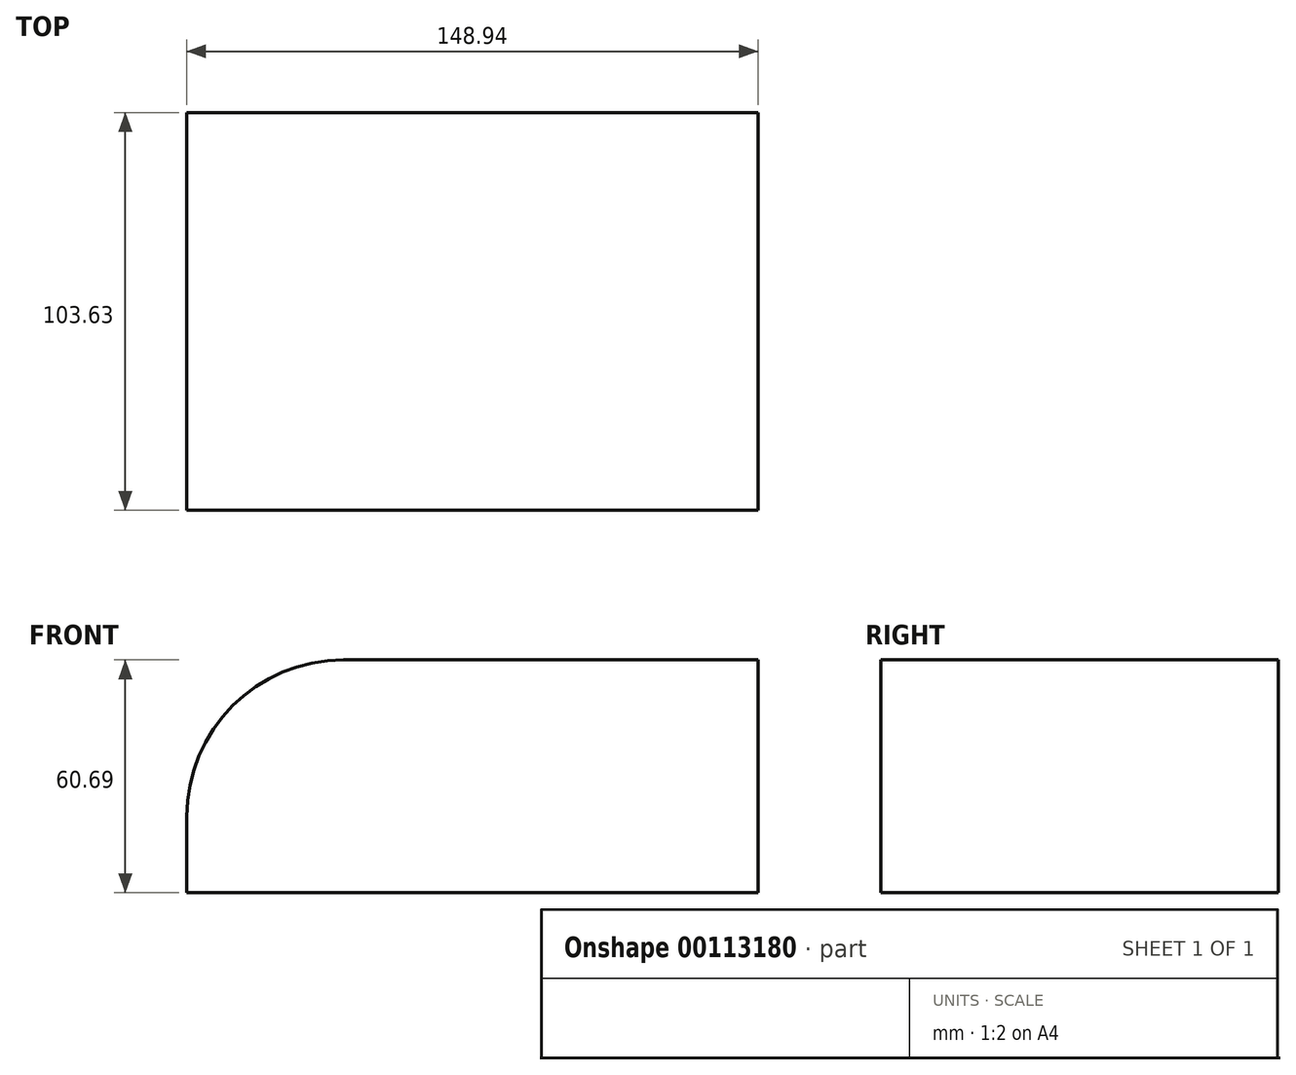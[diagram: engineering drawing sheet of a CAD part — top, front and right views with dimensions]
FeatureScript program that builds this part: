
annotation { "Feature Type Name" : "Feature", "Feature Type Description" : "" }
export const myFeature = defineFeature(function(context is Context, id is Id, definition is map)
    precondition{}
    {
        {
            var Q0;
            Q0=qCreatedBy(makeId("Top.planeOp"),FACE);
            var sketch = newSketch(context, id + "F0", { "sketchPlane" : qUnion([Q0])});
            skLineSegment(sketch, "E0.bottom", {"start": v(-84.58, 52.04) * mm, "end": v(64.36, 52.04) * mm});
            skLineSegment(sketch, "E0.top", {"start": v(-84.58, -51.6) * mm, "end": v(64.36, -51.6) * mm});
            skLineSegment(sketch, "E0.left", {"start": v(-84.58, 52.04) * mm, "end": v(-84.58, -51.6) * mm});
            skLineSegment(sketch, "E0.right", {"start": v(64.36, 52.04) * mm, "end": v(64.36, -51.6) * mm});
            skSolve(sketch);
        }
        {
            var Q0;
            Q0 = qSketchRegion(id + "F0", true);
            extrude(context, id + "F1", {"entities" : qUnion([Q0]), "depth" : 60.69 * mm});
        }
        {
            var Q0;
            Q0=makeQuery(id+"F1.opExtrude","CAP_EDGE",EDGE,{"disambiguationData":[OSD([sQuery(id+"F0.wireOp",EDGE,"E0.left")])],"isStart":false});
            fillet(context, id + "F2", {"entities" : qUnion([Q0]), "radius" : 40.87 * mm, "tangentPropagation" : true, "allowEdgeOverflow" : false});
        }
    });
